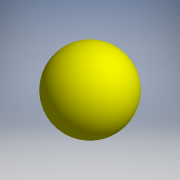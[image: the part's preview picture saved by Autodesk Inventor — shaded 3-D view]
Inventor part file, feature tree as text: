
AUTODESK INVENTOR PART (.ipt)
format: ipt  version: 2017.3 (Build 213256000, 256)  size: 113,664 bytes
history: native  units: mm (DEFAULTED — no unit token found)
features: revolve x1, sketch x1
ambient origin geometry x8: Origin, YZ Plane, XZ Plane, XY Plane, X Axis, Y Axis, Z Axis, Center Point
bodies: Solid1 (feature_tree)
feature tree (2):
  revolve  "Revolution1"  [1 undecoded]
  sketch  "Sketch_1"  dims[d0=360.0deg]
note: 1 required parameter value undecoded (feature->parameter linkage not recoverable at this tier; creation-order binding heuristic only, values carry confidence <= 0.55)
